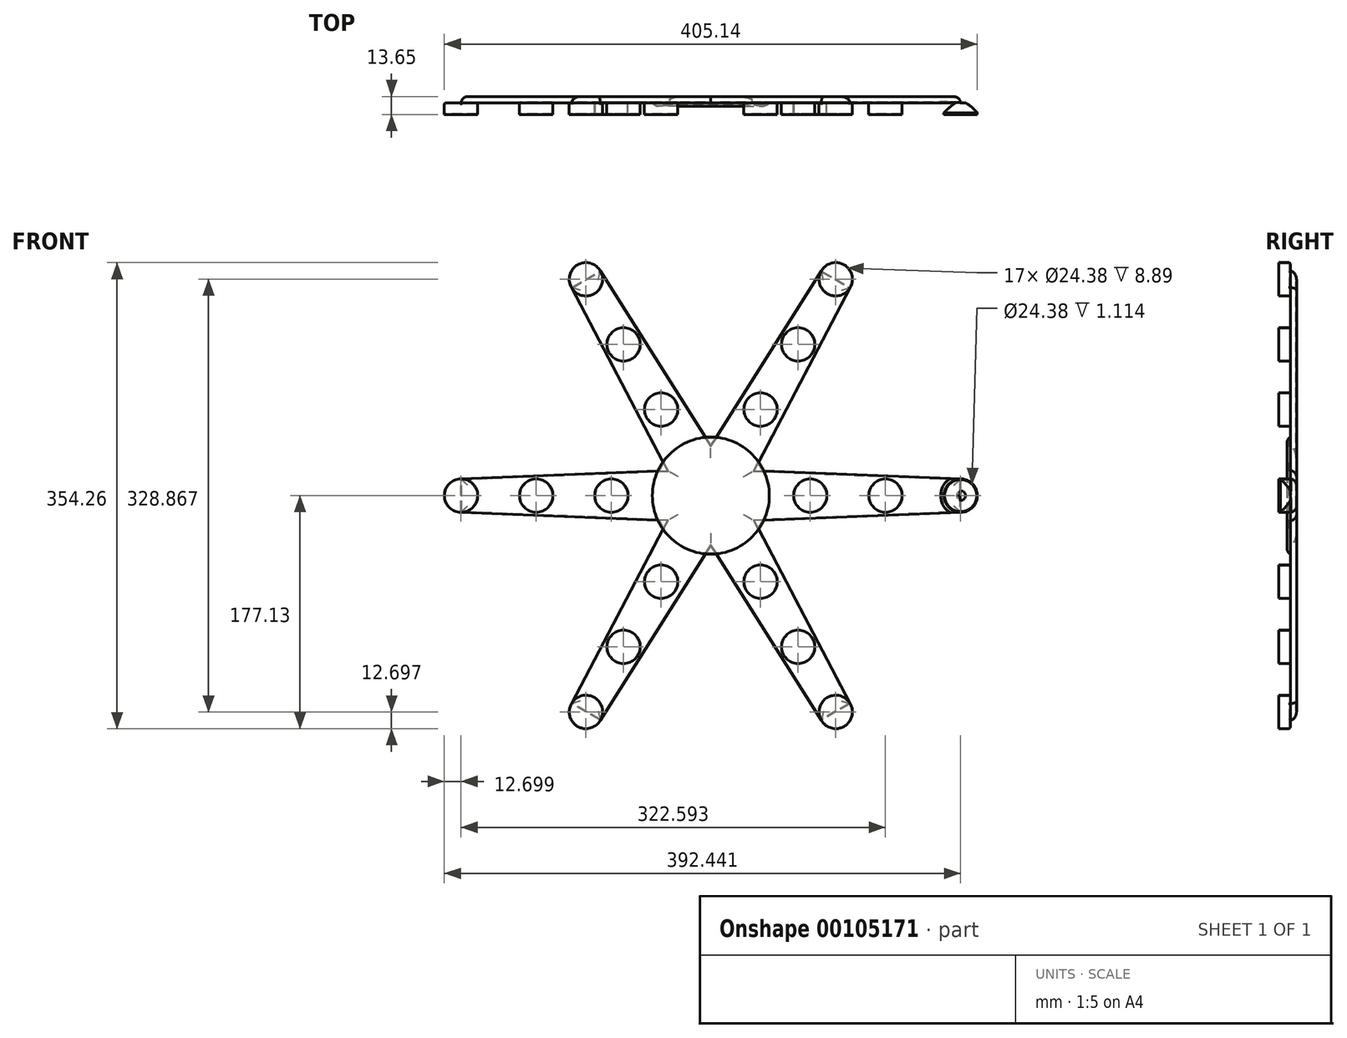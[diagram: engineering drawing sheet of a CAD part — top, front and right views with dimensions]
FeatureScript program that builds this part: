
annotation { "Feature Type Name" : "Feature", "Feature Type Description" : "" }
export const myFeature = defineFeature(function(context is Context, id is Id, definition is map)
    precondition{}
    {
        {
            var Q0;
            Q0=qCreatedBy(makeId("Front.planeOp"),FACE);
            var sketch = newSketch(context, id + "F0", { "sketchPlane" : qUnion([Q0])});
            skCircle(sketch, "E0", {"center": v(0, 0) * mm, "radius": 38.1 * mm});
            skLineSegment(sketch, "E1", {"start": v(-190.5, 0) * mm, "end": v(190.5, 0) * mm, "construction": true});
            skLineSegment(sketch, "E2", {"start": v(0, 190.5) * mm, "end": v(0, -190.5) * mm, "construction": true});
            skLineSegment(sketch, "E3", {"start": v(189.87, 12.7) * mm, "end": v(189.87, -12.7) * mm});
            skLineSegment(sketch, "E4", {"start": v(33, 19.05) * mm, "end": v(189.87, 12.7) * mm});
            skLineSegment(sketch, "E5", {"start": v(189.87, -12.7) * mm, "end": v(33, -19.05) * mm});
            skLineSegment(sketch, "E6.1.0", {"start": v(0, 38.1) * mm, "end": v(83.94, 170.78) * mm});
            skLineSegment(sketch, "E6.1.1", {"start": v(105.93, 158.08) * mm, "end": v(33, 19.05) * mm});
            skLineSegment(sketch, "E6.1.2", {"start": v(83.94, 170.78) * mm, "end": v(105.93, 158.08) * mm});
            skLineSegment(sketch, "E6.2.0", {"start": v(-33, 19.05) * mm, "end": v(-105.93, 158.08) * mm});
            skLineSegment(sketch, "E6.2.1", {"start": v(-83.94, 170.78) * mm, "end": v(0, 38.1) * mm});
            skLineSegment(sketch, "E6.2.2", {"start": v(-105.93, 158.08) * mm, "end": v(-83.94, 170.78) * mm});
            skLineSegment(sketch, "E6.3.0", {"start": v(-33, -19.05) * mm, "end": v(-189.87, -12.7) * mm});
            skLineSegment(sketch, "E6.3.1", {"start": v(-189.87, 12.7) * mm, "end": v(-33, 19.05) * mm});
            skLineSegment(sketch, "E6.3.2", {"start": v(-189.87, -12.7) * mm, "end": v(-189.87, 12.7) * mm});
            skLineSegment(sketch, "E6.4.0", {"start": v(0, -38.1) * mm, "end": v(-83.94, -170.78) * mm});
            skLineSegment(sketch, "E6.4.1", {"start": v(-105.93, -158.08) * mm, "end": v(-33, -19.05) * mm});
            skLineSegment(sketch, "E6.4.2", {"start": v(-83.94, -170.78) * mm, "end": v(-105.93, -158.08) * mm});
            skLineSegment(sketch, "E6.5.0", {"start": v(33, -19.05) * mm, "end": v(105.93, -158.08) * mm});
            skLineSegment(sketch, "E6.5.1", {"start": v(83.94, -170.78) * mm, "end": v(0, -38.1) * mm});
            skLineSegment(sketch, "E6.5.2", {"start": v(105.93, -158.08) * mm, "end": v(83.94, -170.78) * mm});
            skSolve(sketch);
        }
        {
            var Q0;
            Q0 = qSketchRegion(id + "F0", true);
            extrude(context, id + "F1", {"entities" : qUnion([Q0]), "endBound" : BoundingType.SYMMETRIC, "depth" : 4.76 * mm});
        }
        {
            var Q0;
            Q0=makeQuery(id+"F1.opExtrude","CAP_FACE",FACE,{"disambiguationData":[OSD([sQuery(id+"F0.wireOp",EDGE,"E4"),sQuery(id+"F0.wireOp",EDGE,"E3"),sQuery(id+"F0.wireOp",EDGE,"E5"),sQuery(id+"F0.wireOp",EDGE,"E6.1.0"),sQuery(id+"F0.wireOp",EDGE,"E6.1.1"),sQuery(id+"F0.wireOp",EDGE,"E6.1.2"),sQuery(id+"F0.wireOp",EDGE,"E6.2.0"),sQuery(id+"F0.wireOp",EDGE,"E6.2.1"),sQuery(id+"F0.wireOp",EDGE,"E6.2.2"),sQuery(id+"F0.wireOp",EDGE,"E6.3.0"),sQuery(id+"F0.wireOp",EDGE,"E6.3.1"),sQuery(id+"F0.wireOp",EDGE,"E6.3.2"),sQuery(id+"F0.wireOp",EDGE,"E6.4.0"),sQuery(id+"F0.wireOp",EDGE,"E6.4.1"),sQuery(id+"F0.wireOp",EDGE,"E6.4.2"),sQuery(id+"F0.wireOp",EDGE,"E6.5.0"),sQuery(id+"F0.wireOp",EDGE,"E6.5.1"),sQuery(id+"F0.wireOp",EDGE,"E6.5.2")])],"isStart":false});
            var sketch = newSketch(context, id + "F2", { "sketchPlane" : qUnion([Q0])});
            skCircle(sketch, "E7", {"center": v(0, 0) * mm, "radius": 44.45 * mm});
            skSolve(sketch);
        }
        {
            var Q0;
            Q0 = qSketchRegion(id + "F2", true);
            extrude(context, id + "F3", {"entities" : qUnion([Q0]), "operationType" : NewBodyOperationType.ADD, "depth" : 2.54 * mm});
        }
        {
            var Q0;
            {var subQ0=sQuery(id+"F0.wireOp",EDGE,"E5");var subQ2=sQuery(id+"F0.wireOp",EDGE,"E3");var subQ3=sQuery(id+"F0.wireOp",EDGE,"E4");Q0=makeQuery(id+"F3.boolean.opBoolean","SPLIT",FACE,{"disambiguationData":[TD([makeQuery(id+"F1.opExtrude","SWEPT_FACE",FACE,{"disambiguationData":[OSD([subQ3])]})])],"derivedFrom":makeQuery(id+"F1.opExtrude","CAP_FACE",FACE,{"disambiguationData":[OSD([subQ3,subQ2,subQ0,sQuery(id+"F0.wireOp",EDGE,"E6.1.0"),sQuery(id+"F0.wireOp",EDGE,"E6.1.1"),sQuery(id+"F0.wireOp",EDGE,"E6.1.2"),sQuery(id+"F0.wireOp",EDGE,"E6.2.0"),sQuery(id+"F0.wireOp",EDGE,"E6.2.1"),sQuery(id+"F0.wireOp",EDGE,"E6.2.2"),sQuery(id+"F0.wireOp",EDGE,"E6.3.0"),sQuery(id+"F0.wireOp",EDGE,"E6.3.1"),sQuery(id+"F0.wireOp",EDGE,"E6.3.2"),sQuery(id+"F0.wireOp",EDGE,"E6.4.0"),sQuery(id+"F0.wireOp",EDGE,"E6.4.1"),sQuery(id+"F0.wireOp",EDGE,"E6.4.2"),sQuery(id+"F0.wireOp",EDGE,"E6.5.0"),sQuery(id+"F0.wireOp",EDGE,"E6.5.1"),sQuery(id+"F0.wireOp",EDGE,"E6.5.2")])],"isStart":false})});}
            var sketch = newSketch(context, id + "F4", { "sketchPlane" : qUnion([Q0])});
            skCircle(sketch, "E8", {"center": v(189.87, 0) * mm, "radius": 12.7 * mm});
            skCircle(sketch, "E9", {"center": v(132.72, 0) * mm, "radius": 12.7 * mm});
            skCircle(sketch, "E10", {"center": v(75.57, 0) * mm, "radius": 12.7 * mm});
            skCircle(sketch, "E11.1.0", {"center": v(37.79, 65.45) * mm, "radius": 12.7 * mm});
            skCircle(sketch, "E11.1.1", {"center": v(66.36, 114.94) * mm, "radius": 12.7 * mm});
            skCircle(sketch, "E11.1.2", {"center": v(94.94, 164.43) * mm, "radius": 12.7 * mm});
            skCircle(sketch, "E11.2.0", {"center": v(-37.79, 65.45) * mm, "radius": 12.7 * mm});
            skCircle(sketch, "E11.2.1", {"center": v(-66.36, 114.94) * mm, "radius": 12.7 * mm});
            skCircle(sketch, "E11.2.2", {"center": v(-94.94, 164.43) * mm, "radius": 12.7 * mm});
            skCircle(sketch, "E11.3.0", {"center": v(-75.57, 0) * mm, "radius": 12.7 * mm});
            skCircle(sketch, "E11.3.1", {"center": v(-132.72, 0) * mm, "radius": 12.7 * mm});
            skCircle(sketch, "E11.3.2", {"center": v(-189.87, 0) * mm, "radius": 12.7 * mm});
            skCircle(sketch, "E11.4.0", {"center": v(-37.79, -65.45) * mm, "radius": 12.7 * mm});
            skCircle(sketch, "E11.4.1", {"center": v(-66.36, -114.94) * mm, "radius": 12.7 * mm});
            skCircle(sketch, "E11.4.2", {"center": v(-94.94, -164.43) * mm, "radius": 12.7 * mm});
            skCircle(sketch, "E11.5.0", {"center": v(37.79, -65.45) * mm, "radius": 12.7 * mm});
            skCircle(sketch, "E11.5.1", {"center": v(66.36, -114.94) * mm, "radius": 12.7 * mm});
            skCircle(sketch, "E11.5.2", {"center": v(94.94, -164.43) * mm, "radius": 12.7 * mm});
            skPoint(sketch, "E11.center", {"position": v(0, 0) * mm});
            skSolve(sketch);
        }
        {
            var Q0;
            Q0 = qSketchRegion(id + "F4", true);
            extrude(context, id + "F5", {"entities" : qUnion([Q0]), "operationType" : NewBodyOperationType.ADD, "depth" : 8.9 * mm});
        }
        {
            var Q0;
            Q0=makeQuery(id+"F1.opExtrude","CAP_FACE",FACE,{"disambiguationData":[OSD([sQuery(id+"F0.wireOp",EDGE,"E4"),sQuery(id+"F0.wireOp",EDGE,"E3"),sQuery(id+"F0.wireOp",EDGE,"E5"),sQuery(id+"F0.wireOp",EDGE,"E6.1.0"),sQuery(id+"F0.wireOp",EDGE,"E6.1.1"),sQuery(id+"F0.wireOp",EDGE,"E6.1.2"),sQuery(id+"F0.wireOp",EDGE,"E6.2.0"),sQuery(id+"F0.wireOp",EDGE,"E6.2.1"),sQuery(id+"F0.wireOp",EDGE,"E6.2.2"),sQuery(id+"F0.wireOp",EDGE,"E6.3.0"),sQuery(id+"F0.wireOp",EDGE,"E6.3.1"),sQuery(id+"F0.wireOp",EDGE,"E6.3.2"),sQuery(id+"F0.wireOp",EDGE,"E6.4.0"),sQuery(id+"F0.wireOp",EDGE,"E6.4.1"),sQuery(id+"F0.wireOp",EDGE,"E6.4.2"),sQuery(id+"F0.wireOp",EDGE,"E6.5.0"),sQuery(id+"F0.wireOp",EDGE,"E6.5.1"),sQuery(id+"F0.wireOp",EDGE,"E6.5.2")])],"isStart":true});
            fillet(context, id + "F6", {"entities" : qUnion([Q0]), "radius" : 5.08 * mm, "tangentPropagation" : true, "allowEdgeOverflow" : false});
        }
        {
            var Q0;
            Q0=makeQuery(id+"F5.opExtrude","CAP_EDGE",EDGE,{"disambiguationData":[OSD([sQuery(id+"F4.wireOp",EDGE,"E10")])],"isStart":true});
            var Q1;
            Q1=makeQuery(id+"F5.opExtrude","CAP_EDGE",EDGE,{"disambiguationData":[OSD([sQuery(id+"F4.wireOp",EDGE,"E9")])],"isStart":true});
            var Q2;
            {var subQ0=sQuery(id+"F4.wireOp",EDGE,"E8");Q2=makeQuery(id+"F5.boolean.opBoolean","SPLIT",EDGE,{"disambiguationData":[topologyDisambiguationEdgeConnected([makeQuery(id+"F1.opExtrude","CAP_FACE",FACE,{"disambiguationData":[OSD([sQuery(id+"F0.wireOp",EDGE,"E4"),sQuery(id+"F0.wireOp",EDGE,"E3"),sQuery(id+"F0.wireOp",EDGE,"E5"),sQuery(id+"F0.wireOp",EDGE,"E6.1.0"),sQuery(id+"F0.wireOp",EDGE,"E6.1.1"),sQuery(id+"F0.wireOp",EDGE,"E6.1.2"),sQuery(id+"F0.wireOp",EDGE,"E6.2.0"),sQuery(id+"F0.wireOp",EDGE,"E6.2.1"),sQuery(id+"F0.wireOp",EDGE,"E6.2.2"),sQuery(id+"F0.wireOp",EDGE,"E6.3.0"),sQuery(id+"F0.wireOp",EDGE,"E6.3.1"),sQuery(id+"F0.wireOp",EDGE,"E6.3.2"),sQuery(id+"F0.wireOp",EDGE,"E6.4.0"),sQuery(id+"F0.wireOp",EDGE,"E6.4.1"),sQuery(id+"F0.wireOp",EDGE,"E6.4.2"),sQuery(id+"F0.wireOp",EDGE,"E6.5.0"),sQuery(id+"F0.wireOp",EDGE,"E6.5.1"),sQuery(id+"F0.wireOp",EDGE,"E6.5.2")])],"isStart":false})])],"derivedFrom":makeQuery(id+"F5.opExtrude","CAP_EDGE",EDGE,{"disambiguationData":[OSD([subQ0])],"isStart":true})});}
            var Q3;
            {var subQ0=sQuery(id+"F4.wireOp",EDGE,"E11.1.2");Q3=makeQuery(id+"F5.boolean.opBoolean","SPLIT",EDGE,{"disambiguationData":[topologyDisambiguationEdgeConnected([makeQuery(id+"F1.opExtrude","CAP_FACE",FACE,{"disambiguationData":[OSD([sQuery(id+"F0.wireOp",EDGE,"E4"),sQuery(id+"F0.wireOp",EDGE,"E3"),sQuery(id+"F0.wireOp",EDGE,"E5"),sQuery(id+"F0.wireOp",EDGE,"E6.1.0"),sQuery(id+"F0.wireOp",EDGE,"E6.1.1"),sQuery(id+"F0.wireOp",EDGE,"E6.1.2"),sQuery(id+"F0.wireOp",EDGE,"E6.2.0"),sQuery(id+"F0.wireOp",EDGE,"E6.2.1"),sQuery(id+"F0.wireOp",EDGE,"E6.2.2"),sQuery(id+"F0.wireOp",EDGE,"E6.3.0"),sQuery(id+"F0.wireOp",EDGE,"E6.3.1"),sQuery(id+"F0.wireOp",EDGE,"E6.3.2"),sQuery(id+"F0.wireOp",EDGE,"E6.4.0"),sQuery(id+"F0.wireOp",EDGE,"E6.4.1"),sQuery(id+"F0.wireOp",EDGE,"E6.4.2"),sQuery(id+"F0.wireOp",EDGE,"E6.5.0"),sQuery(id+"F0.wireOp",EDGE,"E6.5.1"),sQuery(id+"F0.wireOp",EDGE,"E6.5.2")])],"isStart":false})])],"derivedFrom":makeQuery(id+"F5.opExtrude","CAP_EDGE",EDGE,{"disambiguationData":[OSD([subQ0])],"isStart":true})});}
            var Q4;
            Q4=makeQuery(id+"F5.opExtrude","CAP_EDGE",EDGE,{"disambiguationData":[OSD([sQuery(id+"F4.wireOp",EDGE,"E11.1.1")])],"isStart":true});
            var Q5;
            Q5=makeQuery(id+"F5.opExtrude","CAP_EDGE",EDGE,{"disambiguationData":[OSD([sQuery(id+"F4.wireOp",EDGE,"E11.1.0")])],"isStart":true});
            var Q6;
            {var subQ0=sQuery(id+"F4.wireOp",EDGE,"E11.2.2");Q6=makeQuery(id+"F5.boolean.opBoolean","SPLIT",EDGE,{"disambiguationData":[topologyDisambiguationEdgeConnected([makeQuery(id+"F1.opExtrude","CAP_FACE",FACE,{"disambiguationData":[OSD([sQuery(id+"F0.wireOp",EDGE,"E4"),sQuery(id+"F0.wireOp",EDGE,"E3"),sQuery(id+"F0.wireOp",EDGE,"E5"),sQuery(id+"F0.wireOp",EDGE,"E6.1.0"),sQuery(id+"F0.wireOp",EDGE,"E6.1.1"),sQuery(id+"F0.wireOp",EDGE,"E6.1.2"),sQuery(id+"F0.wireOp",EDGE,"E6.2.0"),sQuery(id+"F0.wireOp",EDGE,"E6.2.1"),sQuery(id+"F0.wireOp",EDGE,"E6.2.2"),sQuery(id+"F0.wireOp",EDGE,"E6.3.0"),sQuery(id+"F0.wireOp",EDGE,"E6.3.1"),sQuery(id+"F0.wireOp",EDGE,"E6.3.2"),sQuery(id+"F0.wireOp",EDGE,"E6.4.0"),sQuery(id+"F0.wireOp",EDGE,"E6.4.1"),sQuery(id+"F0.wireOp",EDGE,"E6.4.2"),sQuery(id+"F0.wireOp",EDGE,"E6.5.0"),sQuery(id+"F0.wireOp",EDGE,"E6.5.1"),sQuery(id+"F0.wireOp",EDGE,"E6.5.2")])],"isStart":false})])],"derivedFrom":makeQuery(id+"F5.opExtrude","CAP_EDGE",EDGE,{"disambiguationData":[OSD([subQ0])],"isStart":true})});}
            var Q7;
            Q7=makeQuery(id+"F5.opExtrude","CAP_EDGE",EDGE,{"disambiguationData":[OSD([sQuery(id+"F4.wireOp",EDGE,"E11.2.1")])],"isStart":true});
            var Q8;
            Q8=makeQuery(id+"F5.opExtrude","CAP_EDGE",EDGE,{"disambiguationData":[OSD([sQuery(id+"F4.wireOp",EDGE,"E11.2.0")])],"isStart":true});
            var Q9;
            {var subQ0=sQuery(id+"F4.wireOp",EDGE,"E11.4.2");Q9=makeQuery(id+"F5.boolean.opBoolean","SPLIT",EDGE,{"disambiguationData":[topologyDisambiguationEdgeConnected([makeQuery(id+"F1.opExtrude","CAP_FACE",FACE,{"disambiguationData":[OSD([sQuery(id+"F0.wireOp",EDGE,"E4"),sQuery(id+"F0.wireOp",EDGE,"E3"),sQuery(id+"F0.wireOp",EDGE,"E5"),sQuery(id+"F0.wireOp",EDGE,"E6.1.0"),sQuery(id+"F0.wireOp",EDGE,"E6.1.1"),sQuery(id+"F0.wireOp",EDGE,"E6.1.2"),sQuery(id+"F0.wireOp",EDGE,"E6.2.0"),sQuery(id+"F0.wireOp",EDGE,"E6.2.1"),sQuery(id+"F0.wireOp",EDGE,"E6.2.2"),sQuery(id+"F0.wireOp",EDGE,"E6.3.0"),sQuery(id+"F0.wireOp",EDGE,"E6.3.1"),sQuery(id+"F0.wireOp",EDGE,"E6.3.2"),sQuery(id+"F0.wireOp",EDGE,"E6.4.0"),sQuery(id+"F0.wireOp",EDGE,"E6.4.1"),sQuery(id+"F0.wireOp",EDGE,"E6.4.2"),sQuery(id+"F0.wireOp",EDGE,"E6.5.0"),sQuery(id+"F0.wireOp",EDGE,"E6.5.1"),sQuery(id+"F0.wireOp",EDGE,"E6.5.2")])],"isStart":false})])],"derivedFrom":makeQuery(id+"F5.opExtrude","CAP_EDGE",EDGE,{"disambiguationData":[OSD([subQ0])],"isStart":true})});}
            var Q10;
            Q10=makeQuery(id+"F5.opExtrude","CAP_EDGE",EDGE,{"disambiguationData":[OSD([sQuery(id+"F4.wireOp",EDGE,"E11.4.1")])],"isStart":true});
            var Q11;
            Q11=makeQuery(id+"F5.opExtrude","CAP_EDGE",EDGE,{"disambiguationData":[OSD([sQuery(id+"F4.wireOp",EDGE,"E11.4.0")])],"isStart":true});
            var Q12;
            {var subQ0=sQuery(id+"F4.wireOp",EDGE,"E11.3.2");Q12=makeQuery(id+"F5.boolean.opBoolean","SPLIT",EDGE,{"disambiguationData":[topologyDisambiguationEdgeConnected([makeQuery(id+"F1.opExtrude","CAP_FACE",FACE,{"disambiguationData":[OSD([sQuery(id+"F0.wireOp",EDGE,"E4"),sQuery(id+"F0.wireOp",EDGE,"E3"),sQuery(id+"F0.wireOp",EDGE,"E5"),sQuery(id+"F0.wireOp",EDGE,"E6.1.0"),sQuery(id+"F0.wireOp",EDGE,"E6.1.1"),sQuery(id+"F0.wireOp",EDGE,"E6.1.2"),sQuery(id+"F0.wireOp",EDGE,"E6.2.0"),sQuery(id+"F0.wireOp",EDGE,"E6.2.1"),sQuery(id+"F0.wireOp",EDGE,"E6.2.2"),sQuery(id+"F0.wireOp",EDGE,"E6.3.0"),sQuery(id+"F0.wireOp",EDGE,"E6.3.1"),sQuery(id+"F0.wireOp",EDGE,"E6.3.2"),sQuery(id+"F0.wireOp",EDGE,"E6.4.0"),sQuery(id+"F0.wireOp",EDGE,"E6.4.1"),sQuery(id+"F0.wireOp",EDGE,"E6.4.2"),sQuery(id+"F0.wireOp",EDGE,"E6.5.0"),sQuery(id+"F0.wireOp",EDGE,"E6.5.1"),sQuery(id+"F0.wireOp",EDGE,"E6.5.2")])],"isStart":false})])],"derivedFrom":makeQuery(id+"F5.opExtrude","CAP_EDGE",EDGE,{"disambiguationData":[OSD([subQ0])],"isStart":true})});}
            var Q13;
            Q13=makeQuery(id+"F5.opExtrude","CAP_EDGE",EDGE,{"disambiguationData":[OSD([sQuery(id+"F4.wireOp",EDGE,"E11.3.1")])],"isStart":true});
            var Q14;
            Q14=makeQuery(id+"F5.opExtrude","CAP_EDGE",EDGE,{"disambiguationData":[OSD([sQuery(id+"F4.wireOp",EDGE,"E11.3.0")])],"isStart":true});
            var Q15;
            Q15=makeQuery(id+"F5.opExtrude","CAP_EDGE",EDGE,{"disambiguationData":[OSD([sQuery(id+"F4.wireOp",EDGE,"E11.5.0")])],"isStart":true});
            var Q16;
            Q16=makeQuery(id+"F5.opExtrude","CAP_EDGE",EDGE,{"disambiguationData":[OSD([sQuery(id+"F4.wireOp",EDGE,"E11.5.1")])],"isStart":true});
            var Q17;
            {var subQ0=sQuery(id+"F4.wireOp",EDGE,"E11.5.2");Q17=makeQuery(id+"F5.boolean.opBoolean","SPLIT",EDGE,{"disambiguationData":[topologyDisambiguationEdgeConnected([makeQuery(id+"F1.opExtrude","CAP_FACE",FACE,{"disambiguationData":[OSD([sQuery(id+"F0.wireOp",EDGE,"E4"),sQuery(id+"F0.wireOp",EDGE,"E3"),sQuery(id+"F0.wireOp",EDGE,"E5"),sQuery(id+"F0.wireOp",EDGE,"E6.1.0"),sQuery(id+"F0.wireOp",EDGE,"E6.1.1"),sQuery(id+"F0.wireOp",EDGE,"E6.1.2"),sQuery(id+"F0.wireOp",EDGE,"E6.2.0"),sQuery(id+"F0.wireOp",EDGE,"E6.2.1"),sQuery(id+"F0.wireOp",EDGE,"E6.2.2"),sQuery(id+"F0.wireOp",EDGE,"E6.3.0"),sQuery(id+"F0.wireOp",EDGE,"E6.3.1"),sQuery(id+"F0.wireOp",EDGE,"E6.3.2"),sQuery(id+"F0.wireOp",EDGE,"E6.4.0"),sQuery(id+"F0.wireOp",EDGE,"E6.4.1"),sQuery(id+"F0.wireOp",EDGE,"E6.4.2"),sQuery(id+"F0.wireOp",EDGE,"E6.5.0"),sQuery(id+"F0.wireOp",EDGE,"E6.5.1"),sQuery(id+"F0.wireOp",EDGE,"E6.5.2")])],"isStart":false})])],"derivedFrom":makeQuery(id+"F5.opExtrude","CAP_EDGE",EDGE,{"disambiguationData":[OSD([subQ0])],"isStart":true})});}
            fillet(context, id + "F7", {"entities" : qUnion([Q0, Q1, Q2, Q3, Q4, Q5, Q6, Q7, Q8, Q9, Q10, Q11, Q12, Q13, Q14, Q15, Q16, Q17]), "radius" : 1.27 * mm, "tangentPropagation" : true, "allowEdgeOverflow" : false});
        }
        {
            var Q0;
            Q0=makeQuery(id+"F3.opExtrude","CAP_EDGE",EDGE,{"disambiguationData":[OSD([sQuery(id+"F2.wireOp",EDGE,"E7")])],"isStart":false});
            fillet(context, id + "F8", {"entities" : qUnion([Q0]), "radius" : 5.08 * mm, "tangentPropagation" : true, "allowEdgeOverflow" : false});
        }
        {
            var Q0;
            Q0=qCreatedBy(makeId("Top.planeOp"),FACE);
            var sketch = newSketch(context, id + "F9", { "sketchPlane" : qUnion([Q0])});
            skLineSegment(sketch, "E12", {"start": v(193.17, -2.03) * mm, "end": v(205.13, -2.03) * mm});
            skLineSegment(sketch, "E13", {"start": v(205.13, -2.03) * mm, "end": v(205.13, -13.33) * mm});
            skArc(sketch, "E14", {"start": v(205.13, -13.33) * mm, "mid": v(199.77, -7.02) * mm, "end": v(193.17, -2.03) * mm});
            skLineSegment(sketch, "E15", {"start": v(189.92, -12.55) * mm, "end": v(189.92, -5.08) * mm, "construction": true});
            skLineSegment(sketch, "E16", {"start": v(5.76, -8.81) * mm, "end": v(-5.71, -8.81) * mm, "construction": true});
            skPoint(sketch, "E16.startSnap0", {"position": v(189.92, -8.81) * mm});
            skLineSegment(sketch, "E17", {"start": v(0, 19.85) * mm, "end": v(0, 39.71) * mm, "construction": true});
            skLineSegment(sketch, "E18.1.0.0", {"start": v(136.02, -2.03) * mm, "end": v(147.98, -2.03) * mm});
            skLineSegment(sketch, "E18.1.0.1", {"start": v(147.98, -2.03) * mm, "end": v(147.98, -13.33) * mm});
            skArc(sketch, "E18.1.0.2", {"start": v(147.98, -13.33) * mm, "mid": v(142.62, -7.02) * mm, "end": v(136.02, -2.03) * mm});
            skLineSegment(sketch, "E18.2.0.0", {"start": v(78.87, -2.03) * mm, "end": v(90.83, -2.03) * mm});
            skLineSegment(sketch, "E18.2.0.1", {"start": v(90.83, -2.03) * mm, "end": v(90.83, -13.33) * mm});
            skArc(sketch, "E18.2.0.2", {"start": v(90.83, -13.33) * mm, "mid": v(85.47, -7.02) * mm, "end": v(78.87, -2.03) * mm});
            skLineSegment(sketch, "E18.direction1", {"start": v(173.61, -34.73) * mm, "end": v(116.46, -34.73) * mm, "construction": true});
            skSolve(sketch);
        }
        {
            var Q0;
            Q0=makeQuery(id+"F9.imprint","IMPRINT",FACE,{"disambiguationData":[TD([[makeQuery(id+"F9.imprint","IMPRINT",EDGE,{"derivedFrom":sQuery(id+"F9.wireOp",EDGE,"E12")}),-1.0]])]});
            var Q1;
            Q1=sQuery(id+"F9.wireOp",EDGE,"E15");
            revolve(context, id + "F10", {"operationType" : NewBodyOperationType.REMOVE, "entities" : qUnion([Q0]), "axis" : qUnion([Q1]), "revolveType" : RevolveType.FULL, "oppositeDirection" : true});
        }
        {
            var Q0;
            Q0=makeQuery(id+"F5.opExtrude","CAP_FACE",FACE,{"disambiguationData":[OSD([sQuery(id+"F4.wireOp",EDGE,"E8")])],"isStart":false});
            shell(context, id + "F11", {"entities" : qUnion([Q0]), "thickness" : 0.5 * mm});
        }
    });
